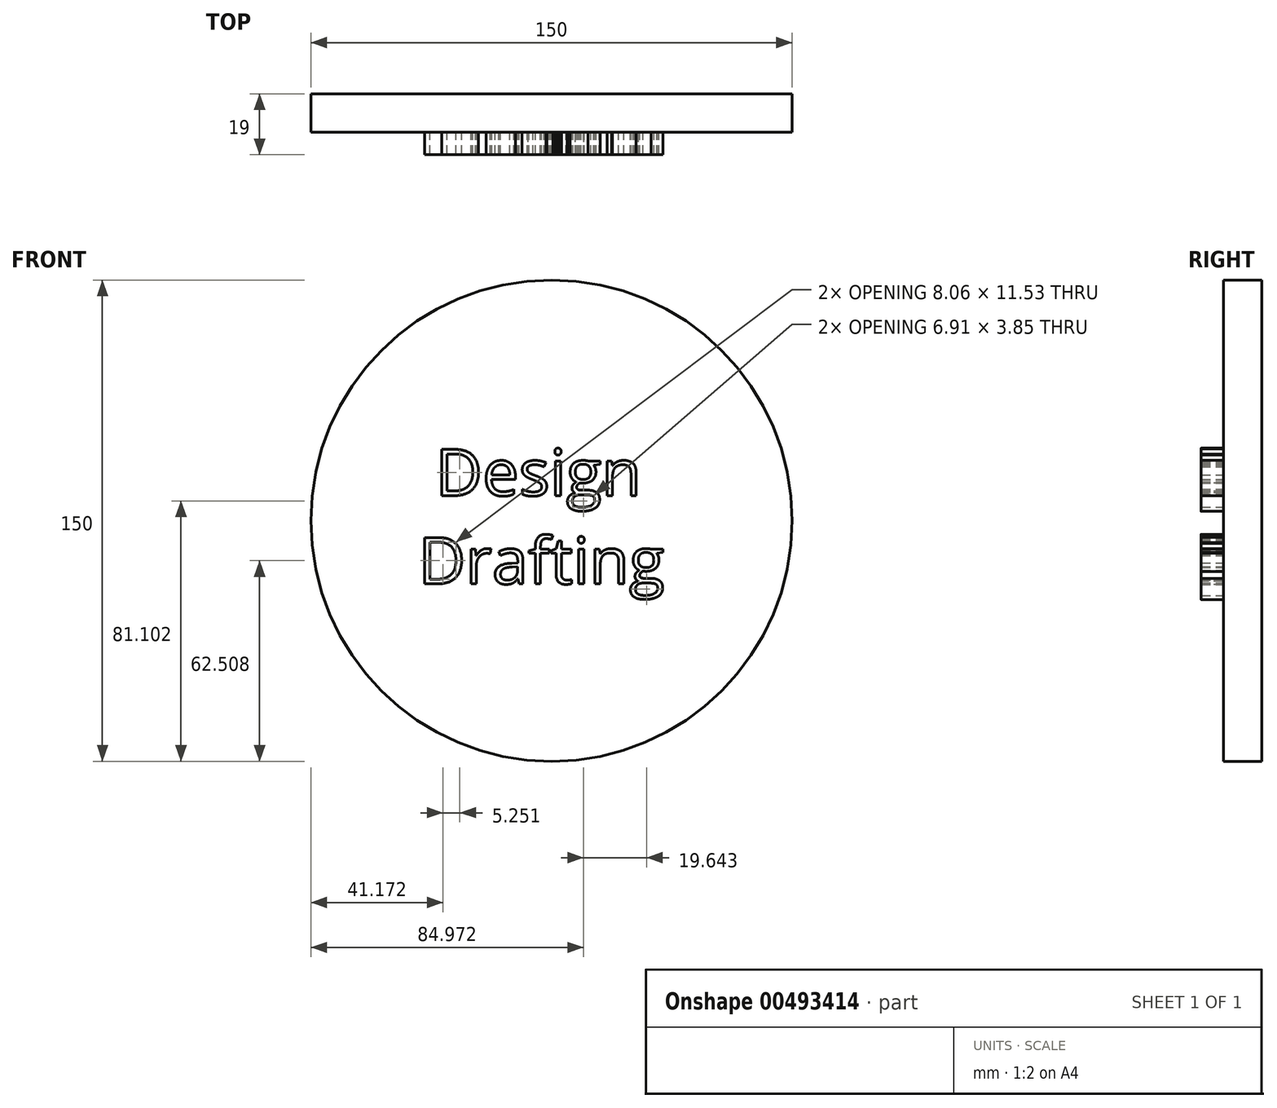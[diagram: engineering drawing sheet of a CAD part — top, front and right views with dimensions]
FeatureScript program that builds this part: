
annotation { "Feature Type Name" : "Feature", "Feature Type Description" : "" }
export const myFeature = defineFeature(function(context is Context, id is Id, definition is map)
    precondition{}
    {
        {
            var Q0;
            Q0=qCreatedBy(makeId("Front.planeOp"),FACE);
            var sketch = newSketch(context, id + "F0", { "sketchPlane" : qUnion([Q0])});
            skCircle(sketch, "E0", {"center": v(0, 0) * mm, "radius": 75 * mm});
            skSolve(sketch);
        }
        {
            var Q0;
            Q0=qCreatedBy(makeId("Front.planeOp"),FACE);
            var sketch = newSketch(context, id + "F1", { "sketchPlane" : qUnion([Q0])});
            skText(sketch, "E1", { "text": " Design \nDrafting", "fontName": "OpenSans-Regular.ttf"});
            const initialGuessF1  = {"E1": [-0.04152, 0.00778, 1, 0, 0.01455]};
            skSetInitialGuess(sketch, initialGuessF1);
            skSolve(sketch);
        }
        {
            var Q0;
            Q0 = qSketchRegion(id + "F1", true);
            extrude(context, id + "F2", {"entities" : qUnion([Q0]), "depth" : 7 * mm});
        }
        {
            var Q0;
            Q0 = qSketchRegion(id + "F0", true);
            extrude(context, id + "F3", {"entities" : qUnion([Q0]), "oppositeDirection" : true, "depth" : 12 * mm});
        }
    });
